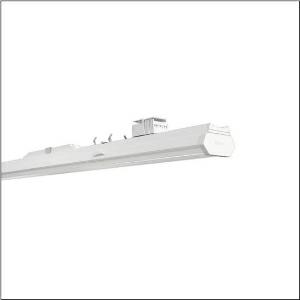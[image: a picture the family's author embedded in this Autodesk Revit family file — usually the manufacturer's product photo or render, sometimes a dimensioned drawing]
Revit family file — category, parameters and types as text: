
# Revit family: licross_r__11_protected_ho_51tp12dn4fxm3c_f4e0
name_source: partatom
category: Lighting Fixtures
units: mm (PartAtom-declared; Revit-internal decimal feet)

## family parameters
Cut with Voids When Loaded = No
Host = Face
Light Source = No
Part Type = Normal
Room Calculation Point = No
Round Connector Dimension = Use Diameter
Shared = No

## types (1)
- --- (1 x LED, 970 lm, 7.4 W, 4000K)
    Apparent Load = 7 VA
    CIE Flux Codes = 70 91 97 98 100
    Color Rendering = 80
    Color Temperature = 4000K
    Default Elevation = 1800 mm
    Description = Licross® 11 Protected HO, luminaire insert, of sheet steel, galvanised, coil coated, white, length: 1.500mm, width: 90mm, height: 101mm, LED rated luminous flux: 15.270lm, light colour: 840, control gear: DALI 2 (for two DALI lines), with plug, 6-pole, with phase selection, for trunking rail, 14-core, mains connection: 220..240V, AC, 50/60Hz, rated input power: 91W, for trunking rail, 14-core, internal wiring halogen-free, for emergency light function, converter,control gear: single battery element, battery: LiFePO4, 9Ah, primary light control with lens, of plastic, primary optical cover: cover, of PMMA, light emission: direct distribution, primary light characteristic: symmetric, protection rating (complete): IP64, insulation class (complete): insulation class I (protective earthing), certification: CE, UKCA, protection symbol: D if used in an environment with conductive dust loads with corresponding accessories, impact resistance: IK06, permissible ambient temperature for indoor applications: +5..+30°C, standard: EN 60598-2-22, LABS conformity tested according to VDMA 24364:2018-05, reducing of maximum allowable ambient temperature of 5°C with ceiling mounting, corresponds to IFS (International Featured Standards) requirements for safety and quality in the food industry, packaging unit: 1 piece
    Height = 92 mm
    Lamp = 1 x LED
    Lamp Light Flux = 970 lm
    Lamp Power = 7.4 W
    Lamp count = 1
    Length = 1500 mm
    Luminous efficacy = 131 lm/W
    Manufacturer = Siteco
    ModVariant = No
    Model = 51TP12DN4FXM3C
    Mounting Place = Ceiling
    Mounting Type = Pendant
    Number of Poles = 1
    OnlyDefault = Yes
    Power Factor = 1
    Product Name = Licross® 11 Protected HO
    Product group = luminaire insert | ceiling pendant
    ProductGroupID = 902
    Protection Class = Protection class I
    Protection Degree = IP 64
    RLX_Detail_Level = 1
    RLX_Emergency_Light_Flux = 0 lm
    RLX_Emergency_Type = 0
    RLX_Emergency_Type_DB = No
    RlxData = <blob elided: 24957 chars, md5=8fc99cc1>
    Socket = socket
    Standby Power = 0 W
    System Light Flux = 970 lm
    System Power = 7 W
    Type Comments = : emergency light operation: 3 h
    Type Image = l_1256148.jpg
    URL = http://relux.com
    VarID = @adj_112453
    Voltage = 0 V
    Weight = 0.00 kg
    Width = 88 mm

## geometry (parser evidence)
native form markers: Blend x4, Sweep x11
no freeform markers — native parametric forms only
